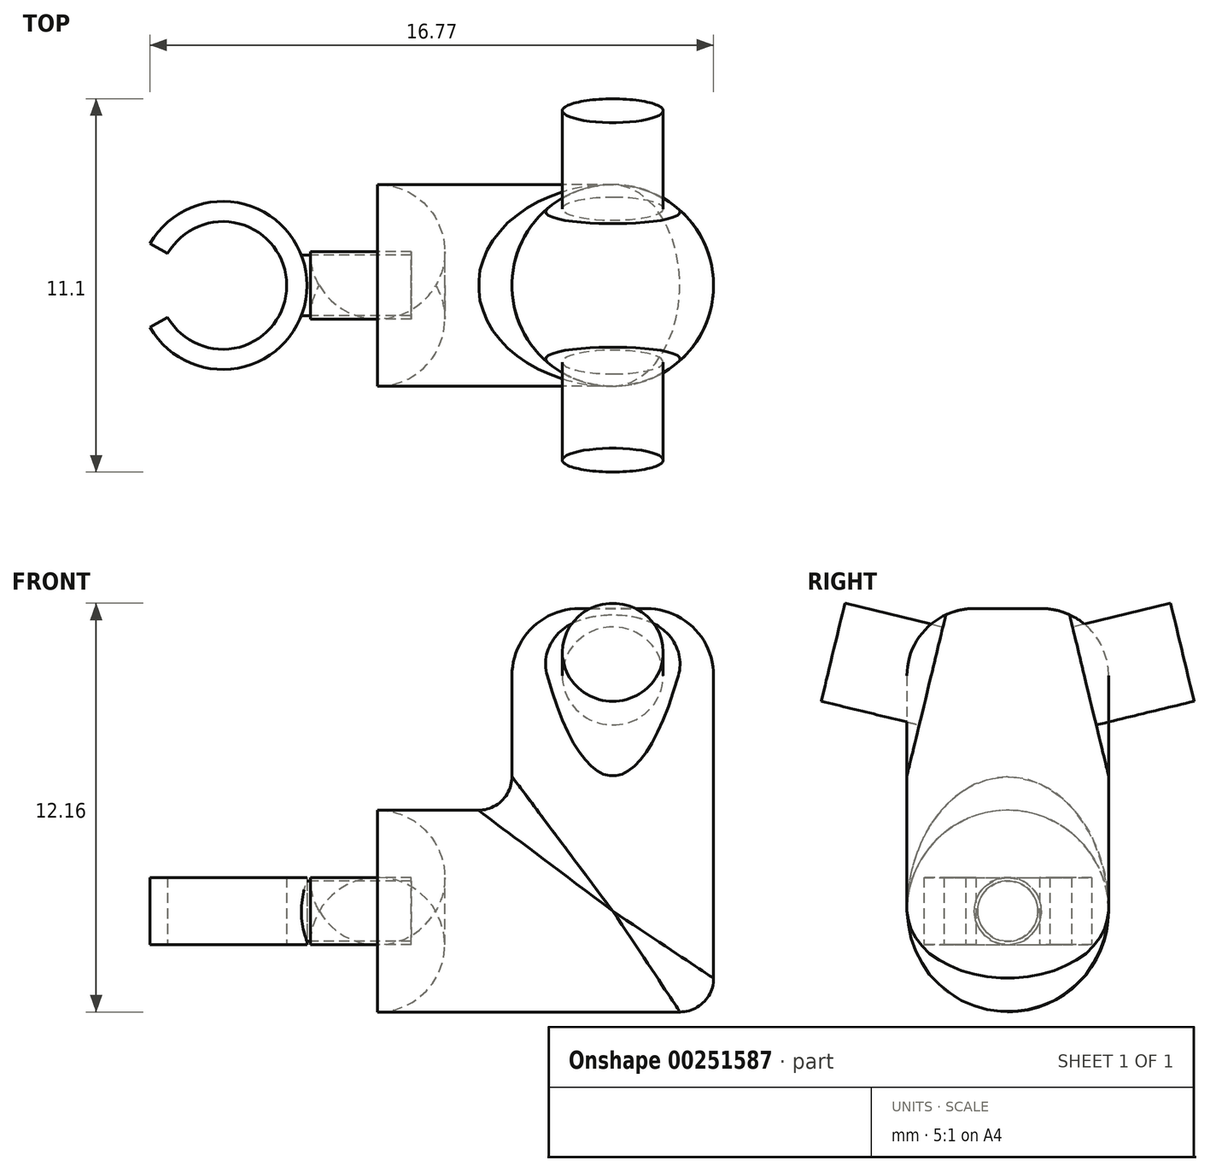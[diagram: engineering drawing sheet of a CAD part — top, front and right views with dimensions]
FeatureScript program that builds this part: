
annotation { "Feature Type Name" : "Feature", "Feature Type Description" : "" }
export const myFeature = defineFeature(function(context is Context, id is Id, definition is map)
    precondition{}
    {
        {
            var Q0;
            Q0=qCreatedBy(makeId("Top.planeOp"),FACE);
            var sketch = newSketch(context, id + "F0", { "sketchPlane" : qUnion([Q0])});
            skCircle(sketch, "E0", {"center": v(0, 0) * mm, "radius": 3 * mm});
            skSolve(sketch);
        }
        {
            var Q0;
            Q0=qCreatedBy(makeId("Front.planeOp"),FACE);
            var sketch = newSketch(context, id + "F1", { "sketchPlane" : qUnion([Q0])});
            skLineSegment(sketch, "E1", {"start": v(-3, 0) * mm, "end": v(-3, -6) * mm});
            skLineSegment(sketch, "E2", {"start": v(-3, -6) * mm, "end": v(-9, -6) * mm});
            skPoint(sketch, "E3", {"position": v(-3, 0) * mm});
            skLineSegment(sketch, "E4", {"start": v(-17.12, -9) * mm, "end": v(5.27, -9) * mm, "construction": true});
            skSolve(sketch);
        }
        {
            var Q0;
            Q0=makeQuery(id+"F0.imprint","IMPRINT",FACE,{"disambiguationData":[TD([[makeQuery(id+"F0.imprint","IMPRINT",EDGE,{"derivedFrom":sQuery(id+"F0.wireOp",EDGE,"E0")}),1.0]])]});
            var Q1;
            Q1=sQuery(id+"F1.wireOp",EDGE,"E1");
            var Q2;
            Q2=sQuery(id+"F1.wireOp",EDGE,"E2");
            sweep(context, id + "F2", {"profiles" : qUnion([Q0]), "path" : qUnion([Q1, Q2])});
        }
        {
            var Q0;
            Q0=makeQuery(id+"F2.opSweep","CAP_FACE",FACE,{"disambiguationData":[OSD([sQuery(id+"F0.wireOp",EDGE,"E0"),sQuery(id+"F1.wireOp",VERTEX,"E1.start")])],"isStart":true});
            fillet(context, id + "F3", {"entities" : qUnion([Q0]), "radius" : 2 * mm, "tangentPropagation" : true, "allowEdgeOverflow" : false});
        }
        {
            var Q0;
            Q0=makeQuery(id+"F2.opSweep","CAP_EDGE",EDGE,{"disambiguationData":[OSD([sQuery(id+"F0.wireOp",EDGE,"E0"),sQuery(id+"F1.wireOp",VERTEX,"E2.end")])],"isStart":false});
            fillet(context, id + "F4", {"entities" : qUnion([Q0]), "radius" : 2 * mm, "tangentPropagation" : true, "allowEdgeOverflow" : false});
        }
        {
            var Q0;
            Q0=makeQuery(id+"F2.opSweep","MID_CAP_EDGE",EDGE,{"disambiguationData":[OSD([sQuery(id+"F0.wireOp",EDGE,"E0"),sQuery(id+"F1.wireOp",VERTEX,"E2.start")])],"capPos":1.0});
            fillet(context, id + "F5", {"entities" : qUnion([Q0]), "radius" : 1 * mm, "tangentPropagation" : true, "allowEdgeOverflow" : false});
        }
        {
            var Q0;
            Q0=makeQuery(id+"F2.opSweep","CAP_FACE",FACE,{"disambiguationData":[OSD([sQuery(id+"F0.wireOp",EDGE,"E0"),sQuery(id+"F1.wireOp",VERTEX,"E2.end")])],"isStart":false});
            var sketch = newSketch(context, id + "F6", { "sketchPlane" : qUnion([Q0])});
            skCircle(sketch, "E5", {"center": v(0, -9) * mm, "radius": 1 * mm});
            skSolve(sketch);
        }
        {
            var Q0;
            Q0=makeQuery(id+"F6.imprint","IMPRINT",FACE,{"disambiguationData":[TD([[makeQuery(id+"F6.imprint","IMPRINT",EDGE,{"derivedFrom":sQuery(id+"F6.wireOp",EDGE,"E5")}),1.0]])]});
            extrude(context, id + "F7", {"entities" : qUnion([Q0]), "operationType" : NewBodyOperationType.REMOVE, "oppositeDirection" : true, "depth" : 3 * mm});
        }
        {
            var Q0;
            Q0=makeQuery(id+"F6.imprint","IMPRINT",FACE,{"disambiguationData":[TD([[makeQuery(id+"F6.imprint","IMPRINT",EDGE,{"derivedFrom":sQuery(id+"F6.wireOp",EDGE,"E5")}),1.0]])]});
            var sketch = newSketch(context, id + "F8", { "sketchPlane" : qUnion([Q0])});
            skPoint(sketch, "E6", {"position": v(0, -9) * mm});
            skCircle(sketch, "E7", {"center": v(0, -9) * mm, "radius": 0.9 * mm});
            skSolve(sketch);
        }
        {
            var Q0;
            Q0=makeQuery(id+"F8.imprint","IMPRINT",FACE,{"disambiguationData":[TD([[makeQuery(id+"F8.imprint","IMPRINT",EDGE,{"derivedFrom":sQuery(id+"F8.wireOp",EDGE,"E7")}),1.0]])]});
            extrude(context, id + "F9", {"entities" : qUnion([Q0]), "oppositeDirection" : true, "depth" : 3 * mm});
        }
        {
            var Q0;
            Q0=qCreatedBy(makeId("Right.planeOp"),FACE);
            var sketch = newSketch(context, id + "F10", { "sketchPlane" : qUnion([Q0])});
            skLineSegment(sketch, "E8", {"start": v(-1.71, 0.33) * mm, "end": v(-3.22, -5.9) * mm});
            skLineSegment(sketch, "E9", {"start": v(-3.22, -5.9) * mm, "end": v(-10.81, -2.6) * mm});
            skLineSegment(sketch, "E10", {"start": v(-10.81, -2.6) * mm, "end": v(-1.71, 0.33) * mm});
            skSolve(sketch);
        }
        {
            var Q0;
            Q0=makeQuery(id+"F10.imprint","IMPRINT",FACE,{"disambiguationData":[TD([[makeQuery(id+"F10.imprint","IMPRINT",EDGE,{"derivedFrom":sQuery(id+"F10.wireOp",EDGE,"E8")}),-1.0]])]});
            extrude(context, id + "F11", {"entities" : qUnion([Q0]), "operationType" : NewBodyOperationType.REMOVE, "endBound" : BoundingType.THROUGH_ALL, "oppositeDirection" : true, "depth" : 25 * mm, "hasSecondDirection" : true, "secondDirectionBound" : SecondDirectionBoundingType.THROUGH_ALL, "secondDirectionOppositeDirection" : false, "secondDirectionDepth" : 25 * mm});
        }
        {
            var Q0;
            Q0=makeQuery(id+"F11.boolean.opBoolean","COPY",FACE,{"derivedFrom":makeQuery(id+"F11.opExtrude","SWEPT_FACE",FACE,{"disambiguationData":[OSD([sQuery(id+"F10.wireOp",EDGE,"E8")])]})});
            var sketch = newSketch(context, id + "F12", { "sketchPlane" : qUnion([Q0])});
            skFitSpline(sketch, "E11", {"points": [v(-3, -1.94) * mm, v(-3, -1.74) * mm, v(-2.94, -1.34) * mm, v(-2.68, -0.79) * mm, v(-2.27, -0.33) * mm, v(-1.77, -0.02) * mm, v(-1.29, 0.15) * mm, v(-0.86, 0.23) * mm, v(-0.43, 0.28) * mm, v(0, 0.3) * mm, v(0.43, 0.28) * mm, v(0.86, 0.23) * mm, v(1.29, 0.15) * mm, v(1.77, -0.02) * mm, v(2.27, -0.33) * mm, v(2.68, -0.79) * mm, v(2.94, -1.34) * mm, v(3, -1.74) * mm, v(3, -1.94) * mm], "construction": true});
            skCircle(sketch, "E12", {"center": v(0, -2.48) * mm, "radius": 1.5 * mm});
            skSolve(sketch);
        }
        {
            var Q0;
            Q0=makeQuery(id+"F12.imprint","IMPRINT",FACE,{"disambiguationData":[TD([[makeQuery(id+"F12.imprint","IMPRINT",EDGE,{"derivedFrom":sQuery(id+"F12.wireOp",EDGE,"E12")}),1.0]])]});
            extrude(context, id + "F13", {"entities" : qUnion([Q0]), "operationType" : NewBodyOperationType.ADD, "depth" : 3 * mm});
        }
        {
            var Q0;
            Q0=sQuery(id+"F1.wireOp",EDGE,"E4");
            cPlane(context, id + "F14", {"entities" : qUnion([Q0]), "cplaneType" : CPlaneType.LINE_ANGLE, "offset" : 25 * mm, "angle" : 90 * degree, "width" : 150 * mm, "height" : 150 * mm});
        }
        {
            var Q0;
            Q0=qCreatedBy(id+"F14.planeOp",FACE);
            var sketch = newSketch(context, id + "F15", { "sketchPlane" : qUnion([Q0])});
            skLineSegment(sketch, "E13.0", {"start": v(-9, -0.9) * mm, "end": v(-9, 0.9) * mm});
            skArc(sketch, "E14", {"start": v(-13.77, -1.25) * mm, "mid": v(-9.1, 0) * mm, "end": v(-13.77, 1.25) * mm});
            skArc(sketch, "E15.0", {"start": v(-13.25, -0.95) * mm, "mid": v(-9.7, 0) * mm, "end": v(-13.25, 0.95) * mm});
            skLineSegment(sketch, "E16", {"start": v(-13.25, 0.95) * mm, "end": v(-13.77, 1.25) * mm});
            skLineSegment(sketch, "E17.MirrorCS", {"start": v(-13.25, -0.95) * mm, "end": v(-13.77, -1.25) * mm});
            skSolve(sketch);
        }
        {
            var Q0;
            Q0=makeQuery(id+"F15.imprint","IMPRINT",FACE,{"disambiguationData":[TD([[makeQuery(id+"F15.imprint","IMPRINT",EDGE,{"derivedFrom":sQuery(id+"F15.wireOp",EDGE,"E14")}),1.0]])]});
            extrude(context, id + "F16", {"entities" : qUnion([Q0]), "endBound" : BoundingType.SYMMETRIC, "depth" : 2 * mm});
        }
        {
            var Q0;
            Q0=makeQuery(id+"F8.imprint","IMPRINT",FACE,{"disambiguationData":[TD([[makeQuery(id+"F8.imprint","IMPRINT",EDGE,{"derivedFrom":sQuery(id+"F8.wireOp",EDGE,"E7")}),1.0]])]});
            var Q1;
            Q1=makeQuery(id+"F16.opExtrude","SWEPT_FACE",FACE,{"disambiguationData":[OSD([sQuery(id+"F15.wireOp",EDGE,"E14")])]});
            extrude(context, id + "F17", {"entities" : qUnion([Q0]), "endBound" : BoundingType.UP_TO_SURFACE, "endBoundEntityFace" : qUnion([Q1]), "depth" : 25 * mm});
        }
        {
            var Q0;
            Q0=makeQuery(id+"F2.opSweep","SWEPT_BODY",BODY,{"disambiguationData":[OSD([sQuery(id+"F0.wireOp",EDGE,"E0"),sQuery(id+"F1.wireOp",EDGE,"E2")])]});
            var Q1;
            Q1=makeQuery(id+"F17.opExtrude","SWEPT_BODY",BODY,{"disambiguationData":[OSD([sQuery(id+"F8.wireOp",EDGE,"E7")])]});
            var Q2;
            Q2=qCreatedBy(makeId("Front.planeOp"),FACE);
            mirror(context, id + "F18", {"entities" : qUnion([Q0, Q1]), "mirrorPlane" : qUnion([Q2])});
        }
    });
